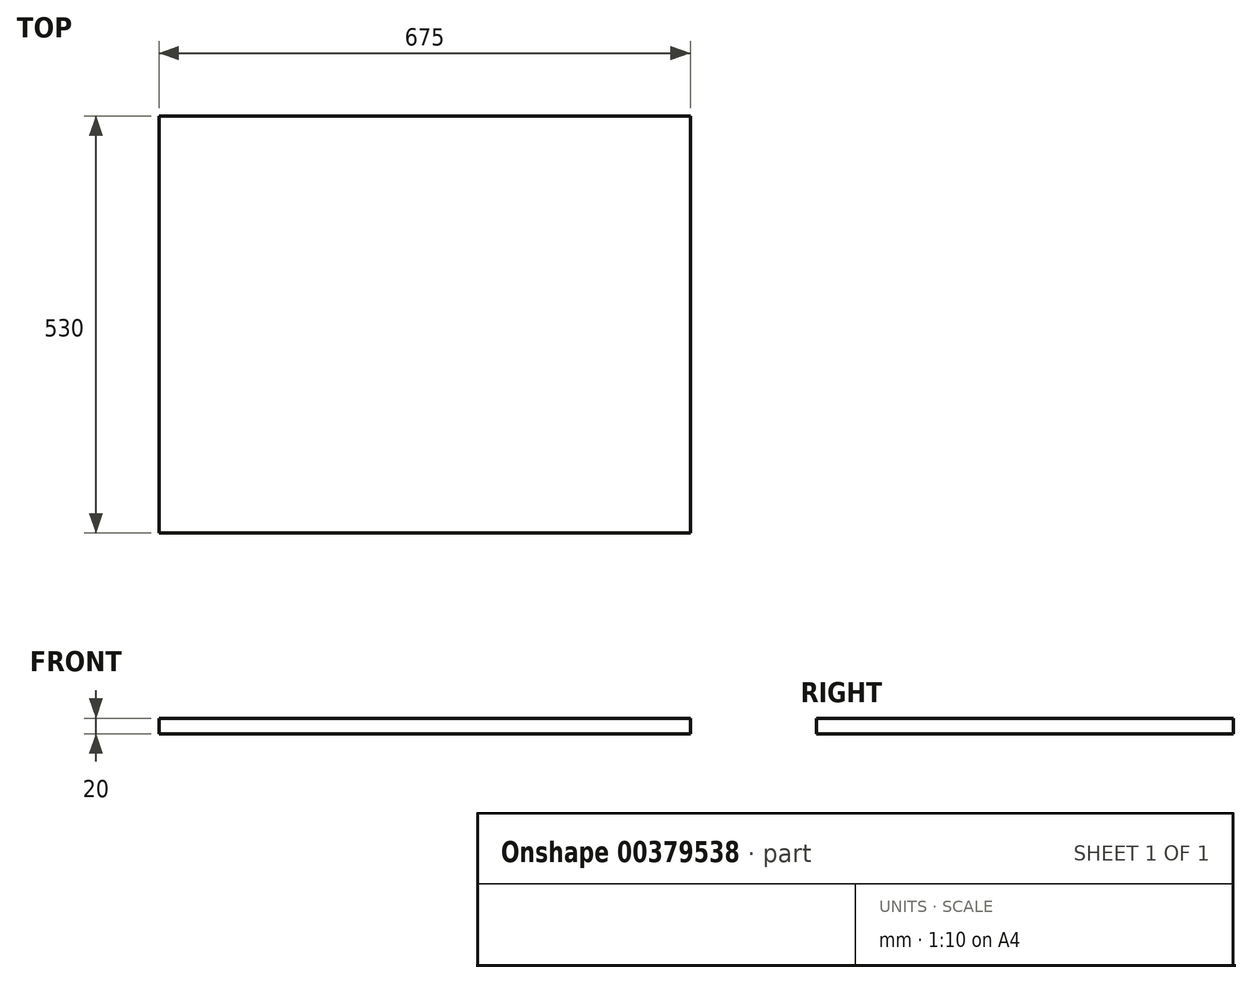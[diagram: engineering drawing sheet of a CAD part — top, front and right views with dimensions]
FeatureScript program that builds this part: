
annotation { "Feature Type Name" : "Feature", "Feature Type Description" : "" }
export const myFeature = defineFeature(function(context is Context, id is Id, definition is map)
    precondition{}
    {
        {
            var Q0;
            Q0=qCreatedBy(makeId("Top.planeOp"),FACE);
            var sketch = newSketch(context, id + "F0", { "sketchPlane" : qUnion([Q0])});
            skLineSegment(sketch, "E0.bottom", {"start": v(-337.5, 265) * mm, "end": v(337.5, 265) * mm});
            skLineSegment(sketch, "E0.top", {"start": v(-337.5, -265) * mm, "end": v(337.5, -265) * mm});
            skLineSegment(sketch, "E0.left", {"start": v(-337.5, 265) * mm, "end": v(-337.5, -265) * mm});
            skLineSegment(sketch, "E0.right", {"start": v(337.5, 265) * mm, "end": v(337.5, -265) * mm});
            skPoint(sketch, "E0.middle", {"position": v(0, 0) * mm});
            skSolve(sketch);
        }
        {
            var Q0;
            Q0=makeQuery(id+"F0.imprint","IMPRINT",FACE,{"disambiguationData":[TD([[makeQuery(id+"F0.imprint","IMPRINT",EDGE,{"derivedFrom":sQuery(id+"F0.wireOp",EDGE,"E0.bottom")}),-1.0]])]});
            extrude(context, id + "F1", {"entities" : qUnion([Q0]), "depth" : 20 * mm});
        }
    });
